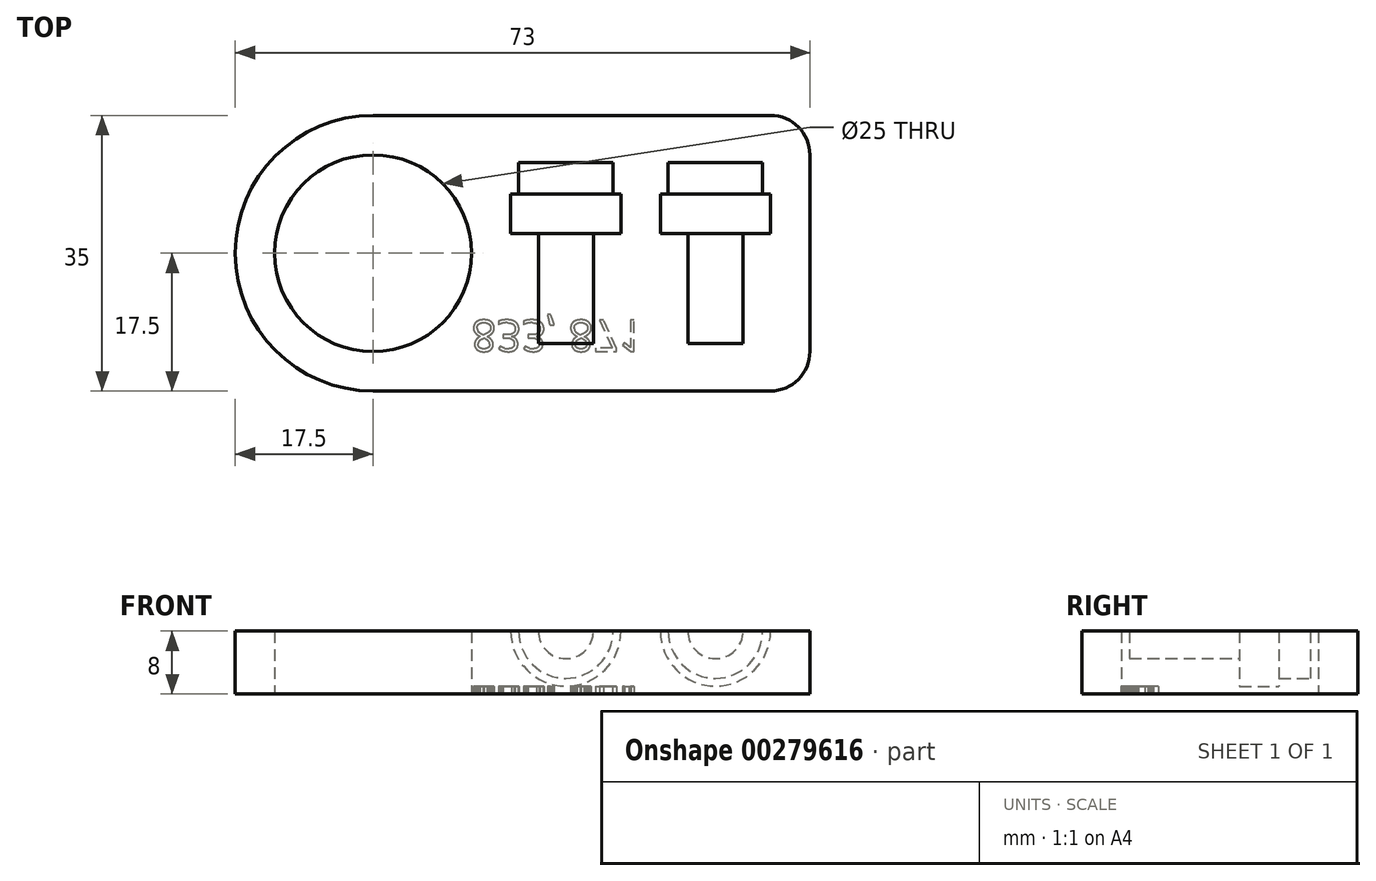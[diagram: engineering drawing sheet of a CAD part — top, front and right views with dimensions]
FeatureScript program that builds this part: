
annotation { "Feature Type Name" : "Feature", "Feature Type Description" : "" }
export const myFeature = defineFeature(function(context is Context, id is Id, definition is map)
    precondition{}
    {
        {
            var Q0;
            Q0=qCreatedBy(makeId("Top.planeOp"),FACE);
            var sketch = newSketch(context, id + "F0", { "sketchPlane" : qUnion([Q0])});
            skLineSegment(sketch, "E0.bottom", {"start": v(17.5, 0) * mm, "end": v(68, 0) * mm});
            skLineSegment(sketch, "E0.top", {"start": v(17.5, 35) * mm, "end": v(68, 35) * mm});
            skLineSegment(sketch, "E0.left", {"start": v(0, 17.5) * mm, "end": v(0, 17.5) * mm});
            skLineSegment(sketch, "E0.right", {"start": v(73, 5) * mm, "end": v(73, 30) * mm});
            skLineSegment(sketch, "E1.bottom", {"start": v(0, 0) * mm, "end": v(17.5, 0) * mm, "construction": true});
            skLineSegment(sketch, "E1.top", {"start": v(0, 17.5) * mm, "end": v(17.5, 17.5) * mm, "construction": true});
            skLineSegment(sketch, "E1.left", {"start": v(0, 0) * mm, "end": v(0, 17.5) * mm, "construction": true});
            skLineSegment(sketch, "E1.right", {"start": v(17.5, 0) * mm, "end": v(17.5, 17.5) * mm, "construction": true});
            skCircle(sketch, "E2", {"center": v(17.5, 17.5) * mm, "radius": 12.5 * mm});
            skPoint(sketch, "E3.visualSharp", {"position": v(0, 0) * mm});
            skArc(sketch, "E3.filletArc", {"start": v(0, 17.5) * mm, "mid": v(5.13, 5.13) * mm, "end": v(17.5, 0) * mm});
            skPoint(sketch, "E4.visualSharp", {"position": v(0, 35) * mm});
            skArc(sketch, "E4.filletArc", {"start": v(17.5, 35) * mm, "mid": v(5.13, 29.87) * mm, "end": v(0, 17.5) * mm});
            skPoint(sketch, "E5.visualSharp", {"position": v(73, 35) * mm});
            skArc(sketch, "E5.filletArc", {"start": v(73, 30) * mm, "mid": v(71.54, 33.54) * mm, "end": v(68, 35) * mm});
            skPoint(sketch, "E6.visualSharp", {"position": v(73, 0) * mm});
            skArc(sketch, "E6.filletArc", {"start": v(68, 0) * mm, "mid": v(71.54, 1.46) * mm, "end": v(73, 5) * mm});
            skSolve(sketch);
        }
        {
            var Q0;
            Q0=makeQuery(id+"F0.imprint","IMPRINT",FACE,{"disambiguationData":[TD([[makeQuery(id+"F0.imprint","IMPRINT",EDGE,{"derivedFrom":sQuery(id+"F0.wireOp",EDGE,"E0.bottom")}),1.0]])]});
            extrude(context, id + "F1", {"entities" : qUnion([Q0]), "depth" : 8 * mm});
        }
        {
            var Q0;
            Q0=makeQuery(id+"F1.opExtrude","CAP_FACE",FACE,{"disambiguationData":[OSD([sQuery(id+"F0.wireOp",EDGE,"E0.bottom"),sQuery(id+"F0.wireOp",EDGE,"E0.top"),sQuery(id+"F0.wireOp",EDGE,"E0.right"),sQuery(id+"F0.wireOp",EDGE,"E2"),sQuery(id+"F0.wireOp",EDGE,"E3.filletArc"),sQuery(id+"F0.wireOp",EDGE,"E4.filletArc"),sQuery(id+"F0.wireOp",EDGE,"E5.filletArc"),sQuery(id+"F0.wireOp",EDGE,"E6.filletArc")])],"isStart":false});
            var sketch = newSketch(context, id + "F2", { "sketchPlane" : qUnion([Q0])});
            skLineSegment(sketch, "E7.bottom", {"start": v(0, 0) * mm, "end": v(42, 0) * mm, "construction": true});
            skLineSegment(sketch, "E7.top", {"start": v(0, 6) * mm, "end": v(42, 6) * mm, "construction": true});
            skLineSegment(sketch, "E7.left", {"start": v(0, 0) * mm, "end": v(0, 6) * mm, "construction": true});
            skLineSegment(sketch, "E7.right", {"start": v(42, 0) * mm, "end": v(42, 6) * mm, "construction": true});
            skLineSegment(sketch, "E8", {"start": v(42, 6) * mm, "end": v(61, 6) * mm, "construction": true});
            skLineSegment(sketch, "E9.bottom", {"start": v(42, 6) * mm, "end": v(45.5, 6) * mm});
            skLineSegment(sketch, "E9.left", {"start": v(42, 6) * mm, "end": v(42, 20) * mm});
            skLineSegment(sketch, "E9.right", {"start": v(45.5, 6) * mm, "end": v(45.5, 20) * mm});
            skLineSegment(sketch, "E10.bottom", {"start": v(45.5, 20) * mm, "end": v(49, 20) * mm});
            skLineSegment(sketch, "E10.top", {"start": v(48, 25) * mm, "end": v(49, 25) * mm});
            skLineSegment(sketch, "E10.left", {"start": v(42, 20) * mm, "end": v(42, 25) * mm});
            skLineSegment(sketch, "E10.right", {"start": v(49, 20) * mm, "end": v(49, 25) * mm});
            skLineSegment(sketch, "E11.top", {"start": v(42, 29) * mm, "end": v(48, 29) * mm});
            skLineSegment(sketch, "E11.left", {"start": v(42, 25) * mm, "end": v(42, 29) * mm});
            skLineSegment(sketch, "E11.right", {"start": v(48, 25) * mm, "end": v(48, 29) * mm});
            skLineSegment(sketch, "E12.bottom", {"start": v(61, 6) * mm, "end": v(64.5, 6) * mm});
            skLineSegment(sketch, "E12.left", {"start": v(61, 6) * mm, "end": v(61, 20) * mm});
            skLineSegment(sketch, "E12.right", {"start": v(64.5, 6) * mm, "end": v(64.5, 20) * mm});
            skLineSegment(sketch, "E13.bottom", {"start": v(64.5, 20) * mm, "end": v(68, 20) * mm});
            skLineSegment(sketch, "E13.top", {"start": v(67, 25) * mm, "end": v(68, 25) * mm});
            skLineSegment(sketch, "E13.left", {"start": v(61, 20) * mm, "end": v(61, 25) * mm});
            skLineSegment(sketch, "E13.right", {"start": v(68, 20) * mm, "end": v(68, 25) * mm});
            skLineSegment(sketch, "E14.top", {"start": v(61, 29) * mm, "end": v(67, 29) * mm});
            skLineSegment(sketch, "E14.left", {"start": v(61, 25) * mm, "end": v(61, 29) * mm});
            skLineSegment(sketch, "E14.right", {"start": v(67, 25) * mm, "end": v(67, 29) * mm});
            skSolve(sketch);
        }
        {
            var Q0;
            Q0=makeQuery(id+"F2.imprint","IMPRINT",FACE,{"disambiguationData":[TD([[makeQuery(id+"F2.imprint","IMPRINT",EDGE,{"derivedFrom":sQuery(id+"F2.wireOp",EDGE,"E9.bottom")}),1.0]])]});
            var Q1;
            Q1=sQuery(id+"F2.wireOp",EDGE,"E10.left");
            revolve(context, id + "F3", {"operationType" : NewBodyOperationType.REMOVE, "entities" : qUnion([Q0]), "axis" : qUnion([Q1]), "revolveType" : RevolveType.FULL, "oppositeDirection" : true});
        }
        {
            var Q0;
            Q0=makeQuery(id+"F2.imprint","IMPRINT",FACE,{"disambiguationData":[TD([[makeQuery(id+"F2.imprint","IMPRINT",EDGE,{"derivedFrom":sQuery(id+"F2.wireOp",EDGE,"E12.bottom")}),1.0]])]});
            var Q1;
            Q1=sQuery(id+"F2.wireOp",EDGE,"E13.left");
            revolve(context, id + "F4", {"operationType" : NewBodyOperationType.REMOVE, "entities" : qUnion([Q0]), "axis" : qUnion([Q1]), "revolveType" : RevolveType.FULL, "oppositeDirection" : true});
        }
        {
            var Q0;
            Q0=makeQuery(id+"F1.opExtrude","CAP_FACE",FACE,{"disambiguationData":[OSD([sQuery(id+"F0.wireOp",EDGE,"E0.bottom"),sQuery(id+"F0.wireOp",EDGE,"E0.top"),sQuery(id+"F0.wireOp",EDGE,"E0.right"),sQuery(id+"F0.wireOp",EDGE,"E2"),sQuery(id+"F0.wireOp",EDGE,"E3.filletArc"),sQuery(id+"F0.wireOp",EDGE,"E4.filletArc"),sQuery(id+"F0.wireOp",EDGE,"E5.filletArc"),sQuery(id+"F0.wireOp",EDGE,"E6.filletArc")])],"isStart":true});
            var sketch = newSketch(context, id + "F5", { "sketchPlane" : qUnion([Q0])});
            skLineSegment(sketch, "E15.bottom", {"start": v(0, 0) * mm, "end": v(30, 0) * mm, "construction": true});
            skLineSegment(sketch, "E15.top", {"start": v(0, -5) * mm, "end": v(30, -5) * mm, "construction": true});
            skLineSegment(sketch, "E15.left", {"start": v(0, 0) * mm, "end": v(0, -5) * mm, "construction": true});
            skLineSegment(sketch, "E15.right", {"start": v(30, 0) * mm, "end": v(30, -5) * mm, "construction": true});
            skText(sketch, "E16", { "text": "833, 871", "fontName": "OpenSans-Regular.ttf"});
            const initialGuessF5  = {"E16": [0.03, -0.009, 1, 0, 0.004]};
            skSetInitialGuess(sketch, initialGuessF5);
            skSolve(sketch);
        }
        {
            var Q0;
            Q0 = qSketchRegion(id + "F5", true);
            extrude(context, id + "F6", {"entities" : qUnion([Q0]), "operationType" : NewBodyOperationType.REMOVE, "oppositeDirection" : true, "depth" : 1 * mm});
        }
    });
